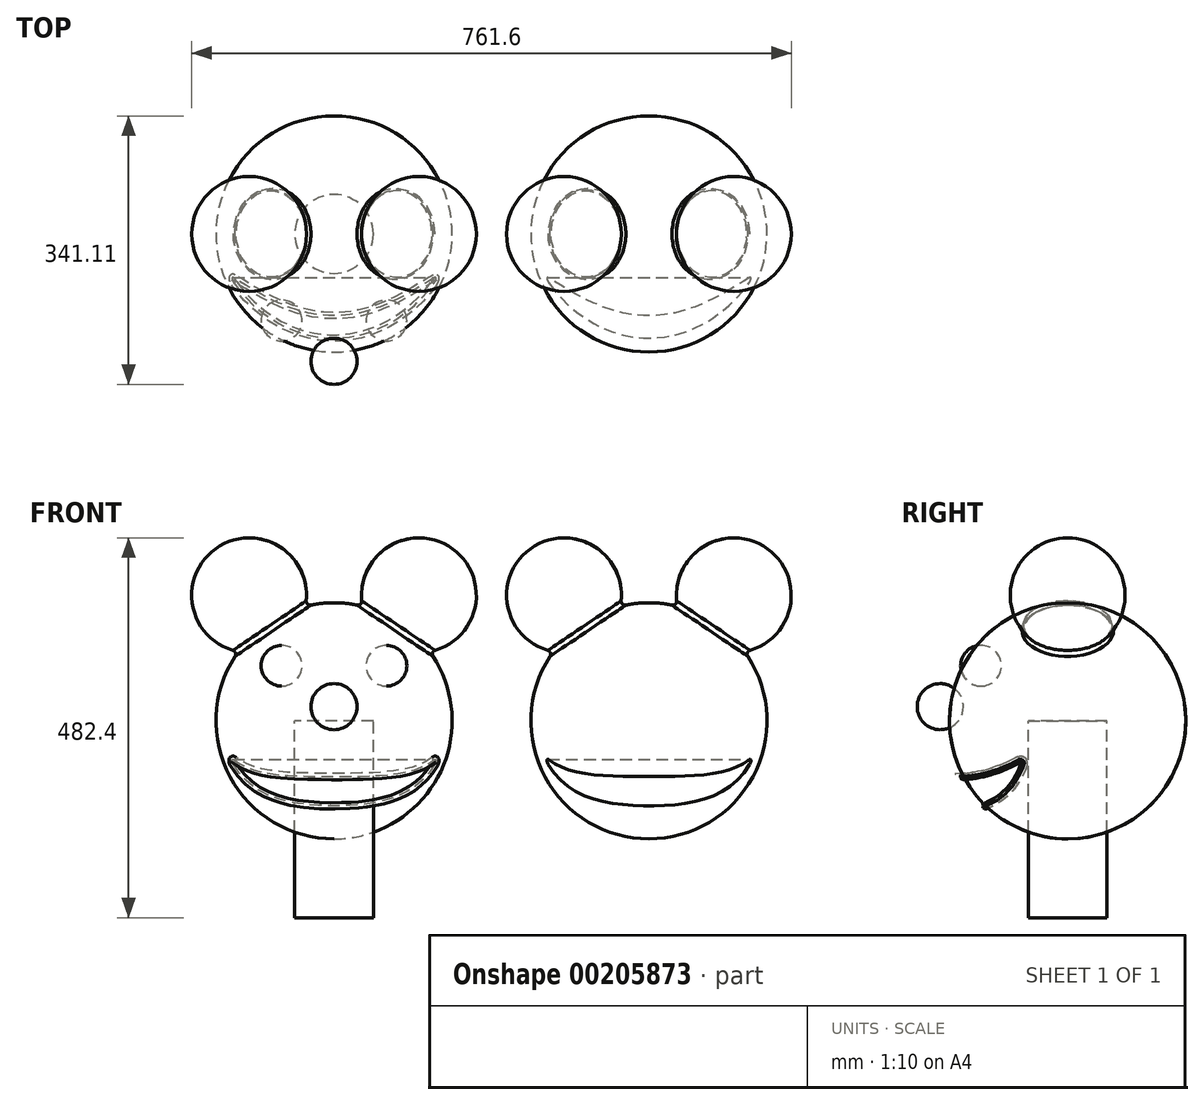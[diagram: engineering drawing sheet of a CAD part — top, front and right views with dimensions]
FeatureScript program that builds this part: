
annotation { "Feature Type Name" : "Feature", "Feature Type Description" : "" }
export const myFeature = defineFeature(function(context is Context, id is Id, definition is map)
    precondition{}
    {
        {
            var Q0;
            Q0=qCreatedBy(makeId("Front.planeOp"),FACE);
            var sketch = newSketch(context, id + "F0", { "sketchPlane" : qUnion([Q0])});
            skCircle(sketch, "E0", {"center": v(0, 0) * mm, "radius": 150 * mm});
            skCircle(sketch, "E1", {"center": v(-107.86, 159.47) * mm, "radius": 72.94 * mm});
            skCircle(sketch, "E2", {"center": v(107.86, 159.47) * mm, "radius": 72.94 * mm});
            skLineSegment(sketch, "E3", {"start": v(0, -180.66) * mm, "end": v(0, 239.02) * mm, "construction": true});
            skLineSegment(sketch, "E4", {"start": v(-107.86, 247.34) * mm, "end": v(-107.86, 63.95) * mm, "construction": true});
            skLineSegment(sketch, "E5", {"start": v(107.86, 252.69) * mm, "end": v(107.86, 55.55) * mm, "construction": true});
            skLineSegment(sketch, "E6", {"start": v(-107.86, 232.4) * mm, "end": v(-107.86, 86.53) * mm});
            skLineSegment(sketch, "E7", {"start": v(107.86, 232.4) * mm, "end": v(107.86, 86.53) * mm});
            skLineSegment(sketch, "E8", {"start": v(0, 150) * mm, "end": v(0, -150) * mm});
            skSolve(sketch);
        }
        {
            var Q0;
            {var subQ0=sQuery(id+"F0.wireOp",EDGE,"E2");var subQ1=sQuery(id+"F0.wireOp",EDGE,"E0");var subQ2=makeQuery(id+"F0.imprint","INTERSECT",VERTEX,{"disambiguationData":[OD(1.0)],"derivedFrom":[subQ1,subQ0]});Q0=makeQuery(id+"F0.imprint","IMPRINT",FACE,{"disambiguationData":[TD([[makeQuery(id+"F0.imprint","IMPRINT",EDGE,{"disambiguationData":[TD([[subQ2,1.0]])],"derivedFrom":subQ1}),1.0]])]});}
            var Q1;
            {var subQ4=sQuery(id+"F0.wireOp",EDGE,"E8");Q1=makeQuery(id+"F0.imprint","IMPRINT",FACE,{"disambiguationData":[TD([[makeQuery(id+"F0.imprint","IMPRINT",EDGE,{"derivedFrom":subQ4}),1.0]])]});}
            var Q2;
            {var subQ0=sQuery(id+"F0.wireOp",EDGE,"E2");var subQ1=sQuery(id+"F0.wireOp",EDGE,"E0");var subQ2=makeQuery(id+"F0.imprint","INTERSECT",VERTEX,{"disambiguationData":[OD(0.0)],"derivedFrom":[subQ1,subQ0]});Q2=makeQuery(id+"F0.imprint","IMPRINT",FACE,{"disambiguationData":[TD([[makeQuery(id+"F0.imprint","IMPRINT",EDGE,{"disambiguationData":[TD([[subQ2,-1.0]])],"derivedFrom":subQ1}),1.0]])]});}
            var Q3;
            Q3=sQuery(id+"F0.wireOp",EDGE,"E3");
            revolve(context, id + "F1", {"entities" : qUnion([Q0, Q1, Q2]), "axis" : qUnion([Q3]), "revolveType" : RevolveType.FULL});
        }
        {
            var Q0;
            {var subQ0=sQuery(id+"F0.wireOp",EDGE,"E1");var subQ1=sQuery(id+"F0.wireOp",EDGE,"E0");var subQ2=makeQuery(id+"F0.imprint","INTERSECT",VERTEX,{"disambiguationData":[OD(1.0)],"derivedFrom":[subQ1,subQ0]});Q0=makeQuery(id+"F0.imprint","IMPRINT",FACE,{"disambiguationData":[TD([[makeQuery(id+"F0.imprint","IMPRINT",EDGE,{"disambiguationData":[TD([[subQ2,1.0]])],"derivedFrom":subQ1}),-1.0]])]});}
            var Q1;
            {var subQ0=sQuery(id+"F0.wireOp",EDGE,"E1");var subQ1=sQuery(id+"F0.wireOp",EDGE,"E0");var subQ2=makeQuery(id+"F0.imprint","INTERSECT",VERTEX,{"disambiguationData":[OD(1.0)],"derivedFrom":[subQ1,subQ0]});Q1=makeQuery(id+"F0.imprint","IMPRINT",FACE,{"disambiguationData":[TD([[makeQuery(id+"F0.imprint","IMPRINT",EDGE,{"disambiguationData":[TD([[subQ2,1.0]])],"derivedFrom":subQ1}),1.0]])]});}
            var Q2;
            Q2=sQuery(id+"F0.wireOp",EDGE,"E4");
            revolve(context, id + "F2", {"entities" : qUnion([Q0, Q1]), "axis" : qUnion([Q2]), "revolveType" : RevolveType.FULL});
        }
        {
            var Q0;
            {var subQ0=sQuery(id+"F0.wireOp",EDGE,"E2");var subQ1=sQuery(id+"F0.wireOp",EDGE,"E0");var subQ2=makeQuery(id+"F0.imprint","INTERSECT",VERTEX,{"disambiguationData":[OD(0.0)],"derivedFrom":[subQ1,subQ0]});Q0=makeQuery(id+"F0.imprint","IMPRINT",FACE,{"disambiguationData":[TD([[makeQuery(id+"F0.imprint","IMPRINT",EDGE,{"disambiguationData":[TD([[subQ2,-1.0]])],"derivedFrom":subQ1}),-1.0]])]});}
            var Q1;
            {var subQ0=sQuery(id+"F0.wireOp",EDGE,"E2");var subQ1=sQuery(id+"F0.wireOp",EDGE,"E0");var subQ2=makeQuery(id+"F0.imprint","INTERSECT",VERTEX,{"disambiguationData":[OD(0.0)],"derivedFrom":[subQ1,subQ0]});Q1=makeQuery(id+"F0.imprint","IMPRINT",FACE,{"disambiguationData":[TD([[makeQuery(id+"F0.imprint","IMPRINT",EDGE,{"disambiguationData":[TD([[subQ2,-1.0]])],"derivedFrom":subQ1}),1.0]])]});}
            var Q2;
            Q2=sQuery(id+"F0.wireOp",EDGE,"E5");
            revolve(context, id + "F3", {"entities" : qUnion([Q0, Q1]), "axis" : qUnion([Q2]), "revolveType" : RevolveType.FULL});
        }
        {
            var Q0;
            Q0=qCreatedBy(makeId("Right.planeOp"),FACE);
            var sketch = newSketch(context, id + "F4", { "sketchPlane" : qUnion([Q0])});
            skCircle(sketch, "E9", {"center": v(-161.83, 18.03) * mm, "radius": 29.27 * mm});
            skLineSegment(sketch, "E10", {"start": v(-161.83, 53.34) * mm, "end": v(-161.83, -21.3) * mm});
            skSolve(sketch);
        }
        {
            var Q0;
            {var subQ0=sQuery(id+"F4.wireOp",EDGE,"E10");var subQ1=sQuery(id+"F4.wireOp",EDGE,"E9");var subQ2=makeQuery(id+"F4.imprint","INTERSECT",VERTEX,{"disambiguationData":[OD(0.0)],"derivedFrom":[subQ1,subQ0]});Q0=makeQuery(id+"F4.imprint","IMPRINT",FACE,{"disambiguationData":[TD([[makeQuery(id+"F4.imprint","IMPRINT",EDGE,{"disambiguationData":[TD([[subQ2,1.0]])],"derivedFrom":subQ1}),1.0]])]});}
            var Q1;
            Q1=sQuery(id+"F4.wireOp",EDGE,"E10");
            revolve(context, id + "F5", {"entities" : qUnion([Q0]), "axis" : qUnion([Q1]), "revolveType" : RevolveType.FULL});
        }
        {
            var Q0;
            Q0=qCreatedBy(makeId("Right.planeOp"),FACE);
            var sketch = newSketch(context, id + "F6", { "sketchPlane" : qUnion([Q0])});
            skCircle(sketch, "E11", {"center": v(0, 0) * mm, "radius": 150 * mm});
            skFitSpline(sketch, "E12", {"points": [v(-132.24, -70.8) * mm, v(-51.68, -42.95) * mm], "startDerivative": vector(87.46, 6.16) * mm, "endDerivative": vector(76.28, 48.34) * mm});
            skFitSpline(sketch, "E13", {"points": [v(-51.68, -42.95) * mm, v(-104.04, -108.05) * mm], "startDerivative": vector(-19.89, -82.34) * mm, "endDerivative": vector(-89.93, -35) * mm});
            skSolve(sketch);
        }
        {
            var Q0;
            {var subQ0=sQuery(id+"F6.wireOp",EDGE,"E12");Q0=makeQuery(id+"F6.imprint","IMPRINT",FACE,{"disambiguationData":[TD([[makeQuery(id+"F6.imprint","IMPRINT",EDGE,{"derivedFrom":subQ0}),-1.0]])]});}
            extrude(context, id + "F7", {"entities" : qUnion([Q0]), "operationType" : NewBodyOperationType.REMOVE, "endBound" : BoundingType.SYMMETRIC, "oppositeDirection" : true, "depth" : 500 * mm});
        }
        {
            var Q0;
            Q0=makeQuery(id+"F7.boolean.opBoolean","COPY",EDGE,{"derivedFrom":makeQuery(id+"F7.opExtrude","SWEPT_EDGE",EDGE,{"disambiguationData":[OSD([sQuery(id+"F6.wireOp",EDGE,"E12"),sQuery(id+"F6.wireOp",EDGE,"E13")])]})});
            fillet(context, id + "F8", {"entities" : qUnion([Q0]), "radius" : 5 * mm, "tangentPropagation" : true, "allowEdgeOverflow" : false});
        }
        {
            var Q0;
            Q0=makeQuery(id+"F7.boolean.opBoolean","INTERSECT",EDGE,{"derivedFrom":[makeQuery(id+"F1.opRevolve","SWEPT_FACE",FACE,{"disambiguationData":[OSD([sQuery(id+"F0.wireOp",EDGE,"E0")])]}),makeQuery(id+"F7.opExtrude","SWEPT_FACE",FACE,{"disambiguationData":[OSD([sQuery(id+"F6.wireOp",EDGE,"E12")])]})]});
            var Q1;
            {var subQ0=sQuery(id+"F6.wireOp",EDGE,"E12");Q1=makeQuery(id+"F8.opFillet","BLEND_VERTEX",VERTEX,{"disambiguationData":[OD(0.0)],"blendedFrom":[makeQuery(id+"F7.boolean.opBoolean","COPY",EDGE,{"derivedFrom":makeQuery(id+"F7.opExtrude","SWEPT_EDGE",EDGE,{"disambiguationData":[OSD([subQ0,sQuery(id+"F6.wireOp",EDGE,"E13")])]})}),makeQuery(id+"F7.boolean.opBoolean","COPY",FACE,{"derivedFrom":makeQuery(id+"F7.opExtrude","SWEPT_FACE",FACE,{"disambiguationData":[OSD([subQ0])]})}),makeQuery(id+"F1.opRevolve","SWEPT_FACE",FACE,{"disambiguationData":[OSD([sQuery(id+"F0.wireOp",EDGE,"E0")])]})],"blendedInto":[makeQuery(id+"F7.boolean.opBoolean","COPY",FACE,{"derivedFrom":makeQuery(id+"F7.opExtrude","SWEPT_FACE",FACE,{"disambiguationData":[OSD([subQ0])]})}),makeQuery(id+"F1.opRevolve","SWEPT_FACE",FACE,{"disambiguationData":[OSD([sQuery(id+"F0.wireOp",EDGE,"E0")])]})]});}
            cPlane(context, id + "F9", {"entities" : qUnion([Q0, Q1]), "cplaneType" : CPlaneType.CURVE_POINT, "offset" : 25 * mm, "width" : 150 * mm, "height" : 150 * mm});
        }
        {
            var Q0;
            Q0=qCreatedBy(id+"F9.planeOp",FACE);
            var sketch = newSketch(context, id + "F10", { "sketchPlane" : qUnion([Q0])});
            skPoint(sketch, "E14.0", {"position": v(-149.45, -12.78) * mm});
            skCircle(sketch, "E15", {"center": v(-149.45, -12.78) * mm, "radius": 4 * mm});
            skSolve(sketch);
        }
        {
            var Q0;
            Q0=qSketchRegion(id+"F10",true);
            var Q1;
            Q1=makeQuery(id+"F7.boolean.opBoolean","INTERSECT",EDGE,{"derivedFrom":[makeQuery(id+"F1.opRevolve","SWEPT_FACE",FACE,{"disambiguationData":[OSD([sQuery(id+"F0.wireOp",EDGE,"E0")])]}),makeQuery(id+"F7.opExtrude","SWEPT_FACE",FACE,{"disambiguationData":[OSD([sQuery(id+"F6.wireOp",EDGE,"E12")])]})]});
            var Q2;
            Q2=makeQuery(id+"F8.opFillet","BLEND_EDGE",EDGE,{"disambiguationData":[OD(1.0)],"blendedFrom":[makeQuery(id+"F7.boolean.opBoolean","COPY",EDGE,{"derivedFrom":makeQuery(id+"F7.opExtrude","SWEPT_EDGE",EDGE,{"disambiguationData":[OSD([sQuery(id+"F6.wireOp",EDGE,"E12"),sQuery(id+"F6.wireOp",EDGE,"E13")])]})}),makeQuery(id+"F1.opRevolve","SWEPT_FACE",FACE,{"disambiguationData":[OSD([sQuery(id+"F0.wireOp",EDGE,"E0")])]})],"blendedInto":[makeQuery(id+"F1.opRevolve","SWEPT_FACE",FACE,{"disambiguationData":[OSD([sQuery(id+"F0.wireOp",EDGE,"E0")])]})]});
            var Q3;
            Q3=makeQuery(id+"F7.boolean.opBoolean","INTERSECT",EDGE,{"derivedFrom":[makeQuery(id+"F1.opRevolve","SWEPT_FACE",FACE,{"disambiguationData":[OSD([sQuery(id+"F0.wireOp",EDGE,"E0")])]}),makeQuery(id+"F7.opExtrude","SWEPT_FACE",FACE,{"disambiguationData":[OSD([sQuery(id+"F6.wireOp",EDGE,"E13")])]})]});
            var Q4;
            Q4=makeQuery(id+"F8.opFillet","BLEND_EDGE",EDGE,{"disambiguationData":[OD(0.0)],"blendedFrom":[makeQuery(id+"F7.boolean.opBoolean","COPY",EDGE,{"derivedFrom":makeQuery(id+"F7.opExtrude","SWEPT_EDGE",EDGE,{"disambiguationData":[OSD([sQuery(id+"F6.wireOp",EDGE,"E12"),sQuery(id+"F6.wireOp",EDGE,"E13")])]})}),makeQuery(id+"F1.opRevolve","SWEPT_FACE",FACE,{"disambiguationData":[OSD([sQuery(id+"F0.wireOp",EDGE,"E0")])]})],"blendedInto":[makeQuery(id+"F1.opRevolve","SWEPT_FACE",FACE,{"disambiguationData":[OSD([sQuery(id+"F0.wireOp",EDGE,"E0")])]})]});
            sweep(context, id + "F11", {"profiles" : qUnion([Q0]), "path" : qUnion([Q1, Q2, Q3, Q4])});
        }
        {
            var Q0;
            Q0=qCreatedBy(makeId("Top.planeOp"),FACE);
            var sketch = newSketch(context, id + "F12", { "sketchPlane" : qUnion([Q0])});
            skCircle(sketch, "E16", {"center": v(0, 0) * mm, "radius": 50 * mm});
            skSolve(sketch);
        }
        {
            var Q0;
            Q0=qSketchRegion(id+"F12",true);
            extrude(context, id + "F13", {"entities" : qUnion([Q0]), "oppositeDirection" : true, "depth" : 250 * mm});
        }
        {
            var Q0;
            Q0=makeQuery(id+"F2.opRevolve","SWEPT_BODY",BODY,{"disambiguationData":[OSD([sQuery(id+"F0.wireOp",EDGE,"E1"),sQuery(id+"F0.wireOp",EDGE,"E6")])]});
            var Q1;
            Q1=makeQuery(id+"F3.opRevolve","SWEPT_BODY",BODY,{"disambiguationData":[OSD([sQuery(id+"F0.wireOp",EDGE,"E2"),sQuery(id+"F0.wireOp",EDGE,"E7")])]});
            var Q2;
            Q2=makeQuery(id+"F1.opRevolve","SWEPT_BODY",BODY,{"disambiguationData":[OSD([sQuery(id+"F0.wireOp",EDGE,"E0"),sQuery(id+"F0.wireOp",EDGE,"E8")])]});
            booleanBodies(context, id + "F14", {"operationType" : BooleanOperationType.UNION, "tools" : qUnion([Q0, Q1, Q2])});
        }
        {
            var Q0;
            Q0=makeQuery(id+"F14.opBoolean","INTERSECT",EDGE,{"derivedFrom":[makeQuery(id+"F2.opRevolve","SWEPT_FACE",FACE,{"disambiguationData":[OSD([sQuery(id+"F0.wireOp",EDGE,"E1")])]}),makeQuery(id+"F1.opRevolve","SWEPT_FACE",FACE,{"disambiguationData":[OSD([sQuery(id+"F0.wireOp",EDGE,"E0")])]})]});
            var Q1;
            Q1=makeQuery(id+"F14.opBoolean","INTERSECT",EDGE,{"derivedFrom":[makeQuery(id+"F3.opRevolve","SWEPT_FACE",FACE,{"disambiguationData":[OSD([sQuery(id+"F0.wireOp",EDGE,"E2")])]}),makeQuery(id+"F1.opRevolve","SWEPT_FACE",FACE,{"disambiguationData":[OSD([sQuery(id+"F0.wireOp",EDGE,"E0")])]})]});
            fillet(context, id + "F15", {"entities" : qUnion([Q0, Q1]), "radius" : 5 * mm, "tangentPropagation" : true, "allowEdgeOverflow" : false});
        }
        {
            var Q0;
            Q0=makeQuery(id+"F2.opRevolve","SWEPT_BODY",BODY,{"disambiguationData":[OSD([sQuery(id+"F0.wireOp",EDGE,"E1"),sQuery(id+"F0.wireOp",EDGE,"E6")])]});
            transform(context, id + "F16", {"entities" : qUnion([Q0]), "transformType" : TransformType.COPY});
        }
        {
            var Q0;
            Q0=makeQuery(id+"F16.opPattern","COPY",BODY,{"derivedFrom":makeQuery(id+"F2.opRevolve","SWEPT_BODY",BODY,{"disambiguationData":[OSD([sQuery(id+"F0.wireOp",EDGE,"E1"),sQuery(id+"F0.wireOp",EDGE,"E6")])]}),"instanceName":"1"});
            transform(context, id + "F17", {"entities" : qUnion([Q0]), "transformType" : TransformType.TRANSLATION_3D, "dx" : 400 * mm, "dy" : 0 * mm, "dz" : 0 * mm, "makeCopy" : false});
        }
        {
            var Q0;
            Q0=qCreatedBy(makeId("Front.planeOp"),FACE);
            cPlane(context, id + "F18", {"entities" : qUnion([Q0]), "cplaneType" : CPlaneType.OFFSET, "offset" : 110 * mm, "width" : 150 * mm, "height" : 150 * mm});
        }
        {
            var Q0;
            Q0=qCreatedBy(id+"F18.planeOp",FACE);
            var sketch = newSketch(context, id + "F19", { "sketchPlane" : qUnion([Q0])});
            skArc(sketch, "E17", {"start": v(-66.57, 95.92) * mm, "mid": v(-92.49, 70) * mm, "end": v(-66.57, 44.08) * mm});
            skArc(sketch, "E18", {"start": v(66.57, 44.08) * mm, "mid": v(92.49, 70) * mm, "end": v(66.57, 95.92) * mm});
            skLineSegment(sketch, "E19", {"start": v(0, -178.42) * mm, "end": v(0, 190.56) * mm, "construction": true});
            skLineSegment(sketch, "E20", {"start": v(-66.57, 31.23) * mm, "end": v(-66.57, 112.55) * mm, "construction": true});
            skLineSegment(sketch, "E21", {"start": v(66.57, 33.93) * mm, "end": v(66.57, 112.69) * mm, "construction": true});
            skLineSegment(sketch, "E22", {"start": v(-66.57, 44.08) * mm, "end": v(-66.57, 95.92) * mm});
            skLineSegment(sketch, "E23", {"start": v(66.57, 44.08) * mm, "end": v(66.57, 95.92) * mm});
            skSolve(sketch);
        }
        {
            var Q0;
            Q0=makeQuery(id+"F19.imprint","IMPRINT",FACE,{"disambiguationData":[TD([[makeQuery(id+"F19.imprint","IMPRINT",EDGE,{"derivedFrom":sQuery(id+"F19.wireOp",EDGE,"E17")}),1.0]])]});
            var Q1;
            Q1=sQuery(id+"F19.wireOp",EDGE,"E20");
            revolve(context, id + "F20", {"entities" : qUnion([Q0]), "axis" : qUnion([Q1]), "revolveType" : RevolveType.FULL});
        }
        {
            var Q0;
            Q0=makeQuery(id+"F19.imprint","IMPRINT",FACE,{"disambiguationData":[TD([[makeQuery(id+"F19.imprint","IMPRINT",EDGE,{"derivedFrom":sQuery(id+"F19.wireOp",EDGE,"E18")}),1.0]])]});
            var Q1;
            Q1=sQuery(id+"F19.wireOp",EDGE,"E21");
            revolve(context, id + "F21", {"entities" : qUnion([Q0]), "axis" : qUnion([Q1]), "revolveType" : RevolveType.FULL});
        }
    });
